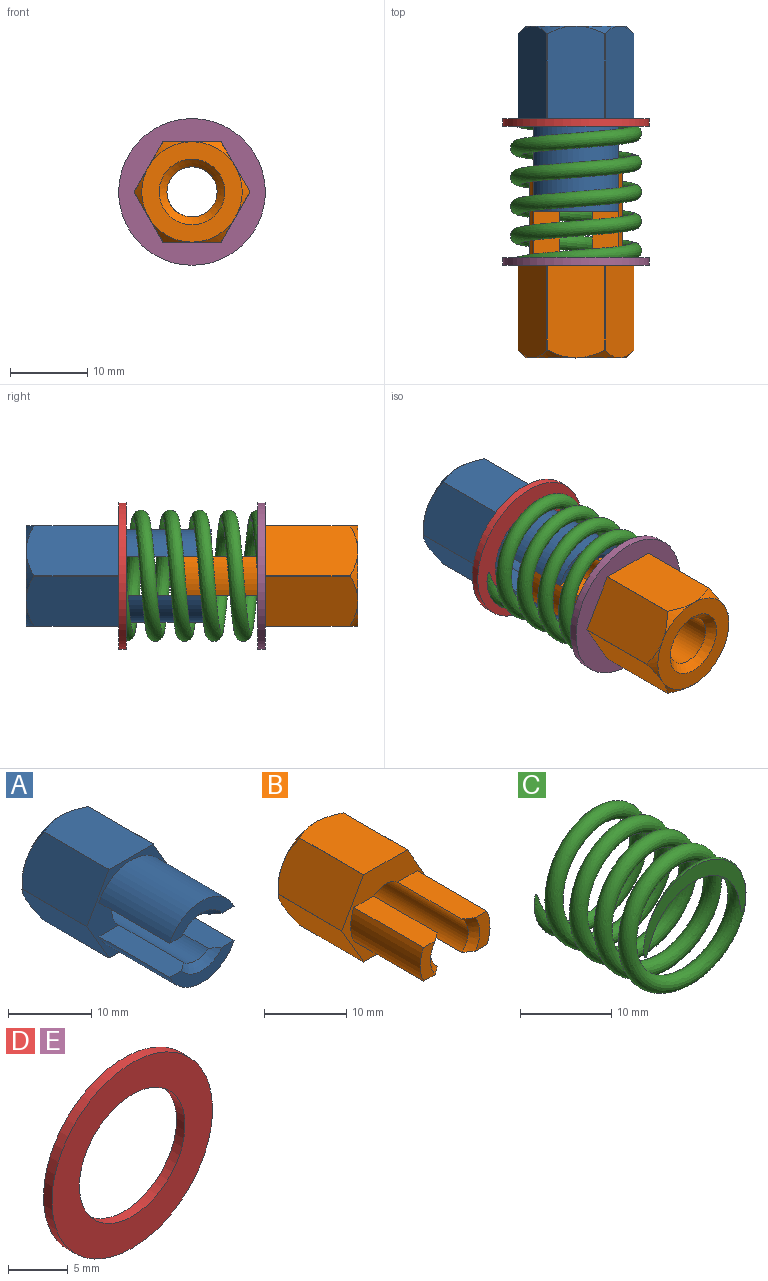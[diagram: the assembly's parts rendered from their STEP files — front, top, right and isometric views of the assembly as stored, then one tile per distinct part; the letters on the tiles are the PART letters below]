
ASSEMBLY  parts=5 mates=5
PART A: 32 faces, bbox 15.2x24.2x15.2 mm
  f0: cylinder r=7.5mm len=11mm, axis (0,1,0), area 0.2mm2, adj f9,f14,f23,f27
  f1: cylinder r=7.5mm len=11mm, axis (0,1,0), area 0.2mm2, adj f13,f14,f15,f27
  f2: cylinder r=7.5mm len=11mm, axis (0,1,0), area 0.2mm2, adj f12,f13,f16,f27
  f3: cylinder r=7.5mm len=11mm, axis (0,1,0), area 0.2mm2, adj f11,f12,f17,f27
  f4: cylinder r=7.5mm len=11mm, axis (0,1,0), area 0.2mm2, adj f10,f11,f18,f27
  f5: cylinder r=3.25mm len=22mm, axis (0,1,0), area 323.7mm2, adj f8,f22,f24,f25,f26,f27,f28,f30
  f6: cylinder r=7.5mm len=11mm, axis (0,1,0), area 0.2mm2, adj f9,f10,f19,f27
  f7: plane 10.91x3.5mm, normal (0,-1,0), area 19mm2, adj f8,f25,f28,f31
  f8: cone r=3.25mm half-angle=45deg, axis (0,-1,0), area 8.7mm2, adj f5,f7,f25,f28
  f9: plane 12.01x7.49mm, normal (0,0,-1), area 87.2mm2, adj f0,f6,f19,f23,f27
  f10: plane 12x6.49mm, normal (0.87,0,-0.5), area 87.2mm2, adj f4,f6,f18,f19,f27
  f11: plane 12x6.49mm, normal (0.87,0,0.5), area 87.2mm2, adj f3,f4,f17,f18,f27
  f12: plane 12.01x7.49mm, normal (0,0,1), area 87.2mm2, adj f2,f3,f16,f17,f27
  f13: plane 12x6.49mm, normal (-0.87,0,0.5), area 87.2mm2, adj f1,f2,f15,f16,f27
  f14: plane 12x6.49mm, normal (-0.87,0,-0.5), area 87.2mm2, adj f0,f1,f15,f23,f27
  f15: cone r=7.5mm half-angle=45deg, axis (0,-1,0), area 3.2mm2, adj f1,f13,f14,f21
  f16: cone r=7.5mm half-angle=45deg, axis (0,-1,0), area 3.2mm2, adj f2,f12,f13,f21
  f17: cone r=7.5mm half-angle=45deg, axis (0,-1,0), area 3.2mm2, adj f3,f11,f12,f21
  f18: cone r=7.5mm half-angle=45deg, axis (0,-1,0), area 3.2mm2, adj f4,f10,f11,f21
  f19: cone r=7.5mm half-angle=45deg, axis (0,-1,0), area 3.2mm2, adj f6,f9,f10,f21
  f20: plane 10.91x3.5mm, normal (0,-1,0), area 19mm2, adj f24,f26,f29,f30
  f21: plane 13x13mm, normal (0,1,0), area 76mm2, adj f15,f16,f17,f18,f19,f22,f23
  f22: cone r=4.25mm half-angle=45deg, axis (0,1,0), area 33.3mm2, adj f5,f21
  f23: cone r=7.5mm half-angle=45deg, axis (0,-1,0), area 3.2mm2, adj f0,f9,f14,f21
  f24: cone r=3.25mm half-angle=45deg, axis (0,-1,0), area 8.7mm2, adj f5,f20,f26,f30
  f25: plane 12.15x3.53mm, normal (0,0,-1), area 39.8mm2, adj f5,f7,f8,f27,f31
  f26: plane 12.15x3.53mm, normal (0,0,1), area 39.8mm2, adj f5,f20,f24,f27,f29
  f27: plane 15x13mm, normal (0,-1,0), area 62.6mm2, adj f0,f1,f2,f3,f4,f5,f6,f9
  f28: plane 12.15x3.53mm, normal (0,0,-1), area 39.8mm2, adj f5,f7,f8,f27,f31
  f29: cylinder r=6mm len=12mm, axis (0,-1,0), area 164.3mm2, adj f20,f26,f27,f30
  f30: plane 12.15x3.53mm, normal (0,0,1), area 39.8mm2, adj f5,f20,f24,f27,f29
  f31: cylinder r=6mm len=12mm, axis (0,-1,0), area 164.3mm2, adj f7,f25,f27,f28
PART B: 32 faces, bbox 15.2x24.2x15.2 mm
  f0: cylinder r=7.5mm len=11mm, axis (0,1,0), area 0.2mm2, adj f10,f15,f24,f27
  f1: cylinder r=7.5mm len=11mm, axis (0,1,0), area 0.2mm2, adj f14,f15,f16,f27
  f2: cylinder r=7.5mm len=11mm, axis (0,1,0), area 0.2mm2, adj f13,f14,f17,f27
  f3: cylinder r=7.5mm len=11mm, axis (0,1,0), area 0.2mm2, adj f12,f13,f18,f27
  f4: cylinder r=7.5mm len=11mm, axis (0,1,0), area 0.2mm2, adj f11,f12,f19,f27
  f5: cylinder r=3.25mm len=22mm, axis (0,1,0), area 350.1mm2, adj f8,f9,f23,f25,f26,f27,f28,f30
  f6: cylinder r=7.5mm len=11mm, axis (0,1,0), area 0.2mm2, adj f10,f11,f20,f27
  f7: plane 5x2.56mm, normal (0,-1,0), area 9.2mm2, adj f9,f28,f29,f30
  f8: cone r=3.25mm half-angle=45deg, axis (0,-1,0), area 7.9mm2, adj f5,f21,f25,f26
  f9: cone r=3.25mm half-angle=45deg, axis (0,-1,0), area 7.9mm2, adj f5,f7,f28,f30
  f10: plane 12.01x7.49mm, normal (0,0,-1), area 87.2mm2, adj f0,f6,f20,f24,f27
  f11: plane 12x6.49mm, normal (0.87,0,-0.5), area 87.2mm2, adj f4,f6,f19,f20,f27
  f12: plane 12x6.49mm, normal (0.87,0,0.5), area 87.2mm2, adj f3,f4,f18,f19,f27
  f13: plane 12.01x7.49mm, normal (0,0,1), area 87.2mm2, adj f2,f3,f17,f18,f27
  f14: plane 12x6.49mm, normal (-0.87,0,0.5), area 87.2mm2, adj f1,f2,f16,f17,f27
  f15: plane 12x6.49mm, normal (-0.87,0,-0.5), area 87.2mm2, adj f0,f1,f16,f24,f27
  f16: cone r=7.5mm half-angle=45deg, axis (0,-1,0), area 3.2mm2, adj f1,f14,f15,f22
  f17: cone r=7.5mm half-angle=45deg, axis (0,-1,0), area 3.2mm2, adj f2,f13,f14,f22
  f18: cone r=7.5mm half-angle=45deg, axis (0,-1,0), area 3.2mm2, adj f3,f12,f13,f22
  f19: cone r=7.5mm half-angle=45deg, axis (0,-1,0), area 3.2mm2, adj f4,f11,f12,f22
  f20: cone r=7.5mm half-angle=45deg, axis (0,-1,0), area 3.2mm2, adj f6,f10,f11,f22
  f21: plane 5x2.56mm, normal (0,-1,0), area 9.2mm2, adj f8,f25,f26,f31
  f22: plane 13x13mm, normal (0,1,0), area 76mm2, adj f16,f17,f18,f19,f20,f23,f24
  f23: cone r=4.25mm half-angle=45deg, axis (0,1,0), area 33.3mm2, adj f5,f22
  f24: cone r=7.5mm half-angle=45deg, axis (0,-1,0), area 3.2mm2, adj f0,f10,f15,f22
  f25: plane 12.15x3.53mm, normal (0,0,1), area 39.8mm2, adj f5,f8,f21,f27,f31
  f26: plane 12.15x3.53mm, normal (0,0,-1), area 39.8mm2, adj f5,f8,f21,f27,f31
  f27: plane 15x13mm, normal (0,-1,0), area 83.9mm2, adj f0,f1,f2,f3,f4,f5,f6,f10
  f28: plane 12.15x3.53mm, normal (0,0,1), area 39.8mm2, adj f5,f7,f9,f27,f29
  f29: cylinder r=6mm len=12mm, axis (0,-1,0), area 61.9mm2, adj f7,f27,f28,f30
  f30: plane 12.15x3.53mm, normal (0,0,-1), area 39.8mm2, adj f5,f7,f9,f27,f29
  f31: cylinder r=6mm len=12mm, axis (0,-1,0), area 61.9mm2, adj f21,f25,f26,f27
PART C: 3 faces, bbox 17.5x21.6x17.6 mm
  f0: bspline ~20.98x16.97mm, area 1324.7mm2, adj f1,f2
  f1: plane 15.82x9.81mm, normal (0,1,0), area 39.1mm2, adj f0
  f2: plane 16.4x10.39mm, normal (0,-1,0), area 37.2mm2, adj f0
PART D: 4 faces, bbox 19x1x19 mm
  f0: cylinder r=6.25mm len=12.5mm, axis (0,1,0), area 39.3mm2, adj f2,f3
  f1: cylinder r=9.5mm len=19mm, axis (0,1,0), area 59.7mm2, adj f2,f3
  f2: plane 19x19mm, normal (0,-1,0), area 160.8mm2, adj f0,f1
  f3: plane 19x19mm, normal (0,1,0), area 160.8mm2, adj f0,f1
PART E: same geometry as D
PLACE A t=(-38.48,13.4,-145.79)mm fixed
PLACE B rot(axis=(1,0,0),180deg) t=(-38.48,-29.6,178.26)mm
PLACE C t=(-103.2,1.4,-56.23)mm
PLACE D t=(-38.92,1.4,-189.54)mm
PLACE E t=(-38.92,-16.6,-189.54)mm
MATE fastened C.f1 <-> D.f2  axis (0,1,0) through (-1.44,0.4,-1.46)mm
MATE fastened E.f0 <-> D.f0  axis (0,1,0) through (-1.89,-16.6,3.74)mm
MATE fastened B.f0 <-> E.f0  axis (0,1,0) through (-1.89,-17.6,3.74)mm
MATE slider A.f0 <-> B.f0  axis (0,-1,0) through (-1.89,-4.6,3.74)mm
MATE fastened D.f0 <-> A.f0  axis (0,1,0) through (-1.89,1.4,3.74)mm
